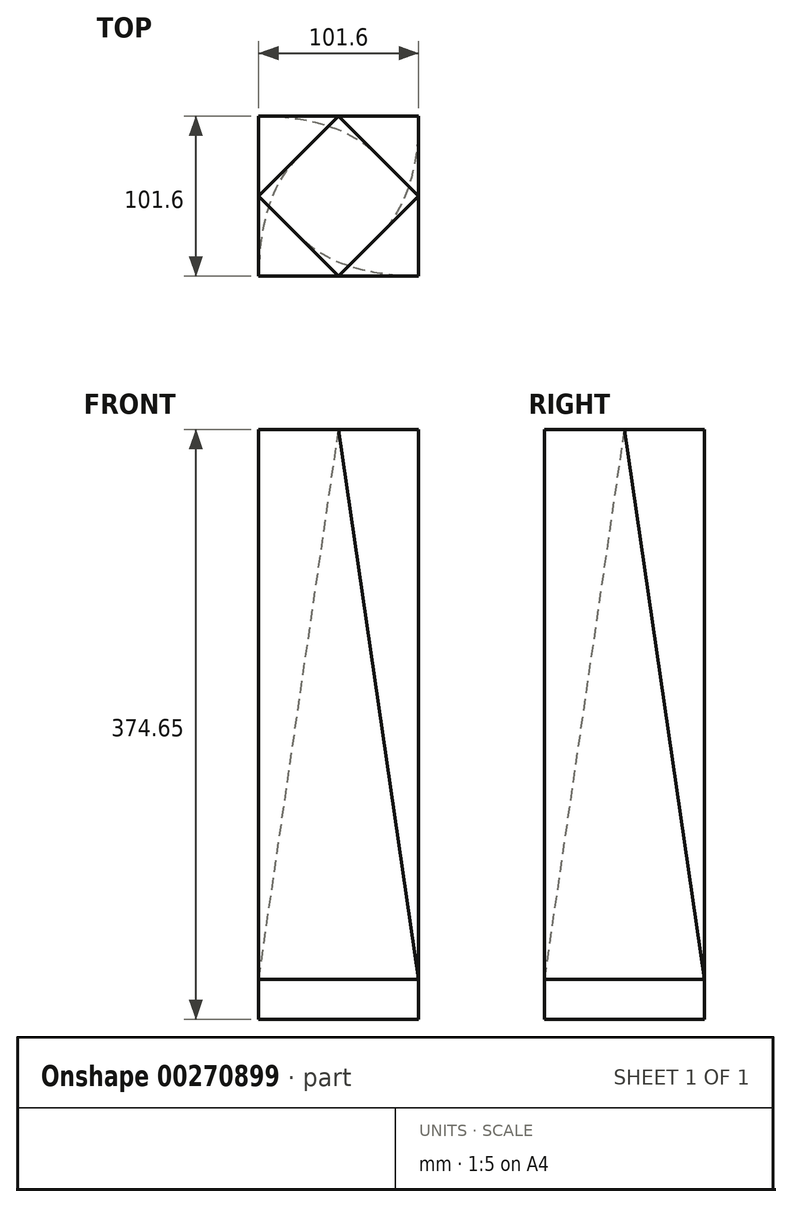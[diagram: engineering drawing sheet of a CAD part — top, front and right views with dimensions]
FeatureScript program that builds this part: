
annotation { "Feature Type Name" : "Feature", "Feature Type Description" : "" }
export const myFeature = defineFeature(function(context is Context, id is Id, definition is map)
    precondition{}
    {
        {
            var Q0;
            Q0=qCreatedBy(makeId("Top.planeOp"),FACE);
            var sketch = newSketch(context, id + "F0", { "sketchPlane" : qUnion([Q0])});
            skLineSegment(sketch, "E0.bottom", {"start": v(0, 0) * mm, "end": v(101.6, 0) * mm});
            skLineSegment(sketch, "E0.top", {"start": v(0, 101.6) * mm, "end": v(101.6, 101.6) * mm});
            skLineSegment(sketch, "E0.left", {"start": v(0, 0) * mm, "end": v(0, 101.6) * mm});
            skLineSegment(sketch, "E0.right", {"start": v(101.6, 0) * mm, "end": v(101.6, 101.6) * mm});
            skSolve(sketch);
        }
        {
            var Q0;
            Q0=makeQuery(id+"F0.imprint","IMPRINT",FACE,{"disambiguationData":[TD([[makeQuery(id+"F0.imprint","IMPRINT",EDGE,{"derivedFrom":sQuery(id+"F0.wireOp",EDGE,"E0.bottom")}),1.0]])]});
            extrude(context, id + "F1", {"entities" : qUnion([Q0]), "depth" : 25.4 * mm});
        }
        {
            var Q0;
            Q0=makeQuery(id+"F1.opExtrude","CAP_FACE",FACE,{"disambiguationData":[OSD([sQuery(id+"F0.wireOp",EDGE,"E0.bottom"),sQuery(id+"F0.wireOp",EDGE,"E0.top"),sQuery(id+"F0.wireOp",EDGE,"E0.left"),sQuery(id+"F0.wireOp",EDGE,"E0.right")])],"isStart":false});
            cPlane(context, id + "F2", {"entities" : qUnion([Q0]), "cplaneType" : CPlaneType.OFFSET, "offset" : 349.25 * mm, "width" : 152.4 * mm, "height" : 152.4 * mm});
        }
        {
            var Q0;
            Q0=qCreatedBy(id+"F2.planeOp",FACE);
            var sketch = newSketch(context, id + "F3", { "sketchPlane" : qUnion([Q0])});
            skPoint(sketch, "E1.0", {"position": v(101.6, 50.8) * mm});
            skLineSegment(sketch, "E2", {"start": v(50.8, 0) * mm, "end": v(0, 50.8) * mm});
            skLineSegment(sketch, "E3", {"start": v(0, 50.8) * mm, "end": v(50.8, 101.6) * mm});
            skLineSegment(sketch, "E4", {"start": v(50.8, 101.6) * mm, "end": v(101.6, 50.8) * mm});
            skLineSegment(sketch, "E5", {"start": v(50.8, 0) * mm, "end": v(101.6, 50.8) * mm});
            skSolve(sketch);
        }
        {
            var Q1;
            Q1=makeQuery(id+"F1.opExtrude","CAP_FACE",FACE,{"disambiguationData":[OSD([sQuery(id+"F0.wireOp",EDGE,"E0.bottom"),sQuery(id+"F0.wireOp",EDGE,"E0.top"),sQuery(id+"F0.wireOp",EDGE,"E0.left"),sQuery(id+"F0.wireOp",EDGE,"E0.right")])],"isStart":false});
            var Q2;
            Q2=makeQuery(id+"F3.imprint","IMPRINT",FACE,{"disambiguationData":[TD([[makeQuery(id+"F3.imprint","IMPRINT",EDGE,{"derivedFrom":sQuery(id+"F3.wireOp",EDGE,"E2")}),-1.0]])]});
            loft(context, id + "F4", {"operationType" : NewBodyOperationType.ADD, "sheetProfilesArray" : [{ "sheetProfileEntities" : qUnion([Q1]) }, { "sheetProfileEntities" : qUnion([Q2]) }]});
        }
    });
